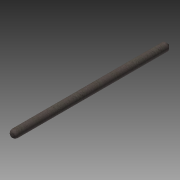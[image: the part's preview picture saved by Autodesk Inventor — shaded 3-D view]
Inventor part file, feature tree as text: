
AUTODESK INVENTOR PART (.ipt)
format: ipt  version: 2015 (Build 190159000, 159)  size: 77,824 bytes
history: native  units: in
note: dims shown in document units (in); Inventor stores cm internally (conversion verified against a paired STEP export)
features: extrude x1, chamfer x1, fillet x1, sketch x1, reference x1
ambient origin geometry x8: Origin, YZ Plane, XZ Plane, XY Plane, X Axis, Y Axis, Z Axis, Center Point
bodies: Solid1 (feature_tree)
feature tree (5):
  extrude  "Extrusion1"  Depth=0.04in TaperAngle=45.0deg
  chamfer  "Chamfer1"  Distance=0.04in
  fillet  "Fillet1"  [1 undecoded]
  sketch  "Sketch1"  dims[d0=2.0in d1=0.0in d2=0.04in d3=0.125in d4=45.0deg d5=0.04in]
  reference  "Reference1"
note: 1 required parameter value undecoded (feature->parameter linkage not recoverable at this tier; creation-order binding heuristic only, values carry confidence <= 0.55)
